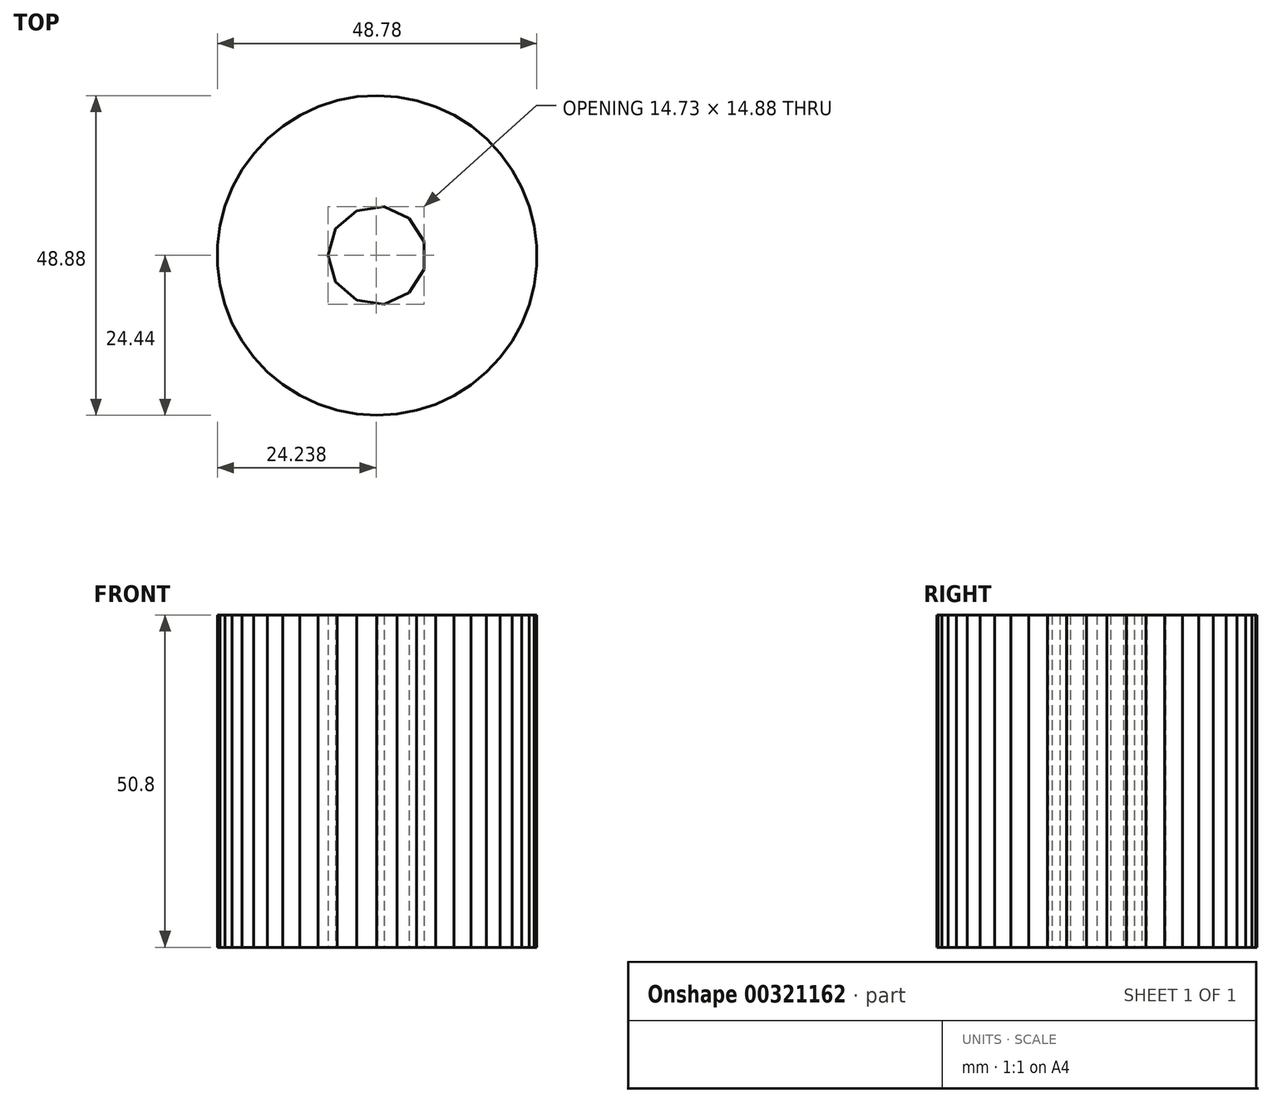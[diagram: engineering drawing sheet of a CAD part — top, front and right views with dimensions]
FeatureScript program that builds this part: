
annotation { "Feature Type Name" : "Feature", "Feature Type Description" : "" }
export const myFeature = defineFeature(function(context is Context, id is Id, definition is map)
    precondition{}
    {
        {
            var Q0;
            Q0=qCreatedBy(makeId("Top.planeOp"),FACE);
            var sketch = newSketch(context, id + "F0", { "sketchPlane" : qUnion([Q0])});
            skCircle(sketch, "E0.cCircle", {"center": v(0, 0) * mm, "radius": 24.4 * mm, "construction": true});
            skLineSegment(sketch, "E0.0", {"start": v(22.1, -10.44) * mm, "end": v(20.61, -13.13) * mm});
            skLineSegment(sketch, "E0.1", {"start": v(20.61, -13.13) * mm, "end": v(18.8, -15.61) * mm});
            skLineSegment(sketch, "E0.2", {"start": v(18.8, -15.61) * mm, "end": v(16.7, -17.84) * mm});
            skLineSegment(sketch, "E0.3", {"start": v(16.7, -17.84) * mm, "end": v(14.33, -19.8) * mm});
            skLineSegment(sketch, "E0.4", {"start": v(14.33, -19.8) * mm, "end": v(11.74, -21.44) * mm});
            skLineSegment(sketch, "E0.5", {"start": v(11.74, -21.44) * mm, "end": v(8.96, -22.74) * mm});
            skLineSegment(sketch, "E0.6", {"start": v(8.96, -22.74) * mm, "end": v(6.04, -23.68) * mm});
            skLineSegment(sketch, "E0.7", {"start": v(6.04, -23.68) * mm, "end": v(3.02, -24.25) * mm});
            skLineSegment(sketch, "E0.8", {"start": v(3.02, -24.25) * mm, "end": v(-0.04, -24.44) * mm});
            skLineSegment(sketch, "E0.9", {"start": v(-0.04, -24.44) * mm, "end": v(-3.1, -24.24) * mm});
            skLineSegment(sketch, "E0.10", {"start": v(-3.1, -24.24) * mm, "end": v(-6.12, -23.66) * mm});
            skLineSegment(sketch, "E0.11", {"start": v(-6.12, -23.66) * mm, "end": v(-9.04, -22.7) * mm});
            skLineSegment(sketch, "E0.12", {"start": v(-9.04, -22.7) * mm, "end": v(-11.8, -21.4) * mm});
            skLineSegment(sketch, "E0.13", {"start": v(-11.8, -21.4) * mm, "end": v(-14.4, -19.75) * mm});
            skLineSegment(sketch, "E0.14", {"start": v(-14.4, -19.75) * mm, "end": v(-16.76, -17.79) * mm});
            skLineSegment(sketch, "E0.15", {"start": v(-16.76, -17.79) * mm, "end": v(-18.86, -15.55) * mm});
            skLineSegment(sketch, "E0.16", {"start": v(-18.86, -15.55) * mm, "end": v(-20.66, -13.06) * mm});
            skLineSegment(sketch, "E0.17", {"start": v(-20.66, -13.06) * mm, "end": v(-22.13, -10.37) * mm});
            skLineSegment(sketch, "E0.18", {"start": v(-22.13, -10.37) * mm, "end": v(-23.26, -7.51) * mm});
            skLineSegment(sketch, "E0.19", {"start": v(-23.26, -7.51) * mm, "end": v(-24.01, -4.54) * mm});
            skLineSegment(sketch, "E0.20", {"start": v(-24.01, -4.54) * mm, "end": v(-24.4, -1.5) * mm});
            skLineSegment(sketch, "E0.21", {"start": v(-24.4, -1.5) * mm, "end": v(-24.39, 1.58) * mm});
            skLineSegment(sketch, "E0.22", {"start": v(-24.39, 1.58) * mm, "end": v(-24, 4.62) * mm});
            skLineSegment(sketch, "E0.23", {"start": v(-24, 4.62) * mm, "end": v(-23.23, 7.6) * mm});
            skLineSegment(sketch, "E0.24", {"start": v(-23.23, 7.6) * mm, "end": v(-22.1, 10.44) * mm});
            skLineSegment(sketch, "E0.25", {"start": v(-22.1, 10.44) * mm, "end": v(-20.61, 13.13) * mm});
            skLineSegment(sketch, "E0.26", {"start": v(-20.61, 13.13) * mm, "end": v(-18.8, 15.61) * mm});
            skLineSegment(sketch, "E0.27", {"start": v(-18.8, 15.61) * mm, "end": v(-16.7, 17.84) * mm});
            skLineSegment(sketch, "E0.28", {"start": v(-16.7, 17.84) * mm, "end": v(-14.33, 19.8) * mm});
            skLineSegment(sketch, "E0.29", {"start": v(-14.33, 19.8) * mm, "end": v(-11.74, 21.44) * mm});
            skLineSegment(sketch, "E0.30", {"start": v(-11.74, 21.44) * mm, "end": v(-8.96, 22.74) * mm});
            skLineSegment(sketch, "E0.31", {"start": v(-8.96, 22.74) * mm, "end": v(-6.04, 23.68) * mm});
            skLineSegment(sketch, "E0.32", {"start": v(-6.04, 23.68) * mm, "end": v(-3.02, 24.25) * mm});
            skLineSegment(sketch, "E0.33", {"start": v(-3.02, 24.25) * mm, "end": v(0.04, 24.44) * mm});
            skLineSegment(sketch, "E0.34", {"start": v(0.04, 24.44) * mm, "end": v(3.1, 24.24) * mm});
            skLineSegment(sketch, "E0.35", {"start": v(3.1, 24.24) * mm, "end": v(6.12, 23.66) * mm});
            skLineSegment(sketch, "E0.36", {"start": v(6.12, 23.66) * mm, "end": v(9.04, 22.7) * mm});
            skLineSegment(sketch, "E0.37", {"start": v(9.04, 22.7) * mm, "end": v(11.8, 21.4) * mm});
            skLineSegment(sketch, "E0.38", {"start": v(11.8, 21.4) * mm, "end": v(14.4, 19.75) * mm});
            skLineSegment(sketch, "E0.39", {"start": v(14.4, 19.75) * mm, "end": v(16.76, 17.79) * mm});
            skLineSegment(sketch, "E0.40", {"start": v(16.76, 17.79) * mm, "end": v(18.86, 15.55) * mm});
            skLineSegment(sketch, "E0.41", {"start": v(18.86, 15.55) * mm, "end": v(20.66, 13.06) * mm});
            skLineSegment(sketch, "E0.42", {"start": v(20.66, 13.06) * mm, "end": v(22.13, 10.37) * mm});
            skLineSegment(sketch, "E0.43", {"start": v(22.13, 10.37) * mm, "end": v(23.26, 7.51) * mm});
            skLineSegment(sketch, "E0.44", {"start": v(23.26, 7.51) * mm, "end": v(24.01, 4.54) * mm});
            skLineSegment(sketch, "E0.45", {"start": v(24.01, 4.54) * mm, "end": v(24.4, 1.5) * mm});
            skLineSegment(sketch, "E0.46", {"start": v(24.4, 1.5) * mm, "end": v(24.39, -1.58) * mm});
            skLineSegment(sketch, "E0.47", {"start": v(24.39, -1.58) * mm, "end": v(24, -4.62) * mm});
            skLineSegment(sketch, "E0.48", {"start": v(24, -4.62) * mm, "end": v(23.23, -7.6) * mm});
            skLineSegment(sketch, "E0.49", {"start": v(23.23, -7.6) * mm, "end": v(22.1, -10.44) * mm});
            skPoint(sketch, "E0.0.midPoint", {"position": v(21.35, -11.79) * mm});
            skCircle(sketch, "E1.cCircle", {"center": v(0, 0) * mm, "radius": 7.21 * mm, "construction": true});
            skLineSegment(sketch, "E1.0", {"start": v(7.21, 2.12) * mm, "end": v(7.21, -2.12) * mm});
            skLineSegment(sketch, "E1.1", {"start": v(7.21, -2.12) * mm, "end": v(4.92, -5.68) * mm});
            skLineSegment(sketch, "E1.2", {"start": v(4.92, -5.68) * mm, "end": v(1.07, -7.44) * mm});
            skLineSegment(sketch, "E1.3", {"start": v(1.07, -7.44) * mm, "end": v(-3.12, -6.84) * mm});
            skLineSegment(sketch, "E1.4", {"start": v(-3.12, -6.84) * mm, "end": v(-6.32, -4.06) * mm});
            skLineSegment(sketch, "E1.5", {"start": v(-6.32, -4.06) * mm, "end": v(-7.52, 0) * mm});
            skLineSegment(sketch, "E1.6", {"start": v(-7.52, 0) * mm, "end": v(-6.32, 4.06) * mm});
            skLineSegment(sketch, "E1.7", {"start": v(-6.32, 4.06) * mm, "end": v(-3.12, 6.84) * mm});
            skLineSegment(sketch, "E1.8", {"start": v(-3.12, 6.84) * mm, "end": v(1.07, 7.44) * mm});
            skLineSegment(sketch, "E1.9", {"start": v(1.07, 7.44) * mm, "end": v(4.92, 5.68) * mm});
            skLineSegment(sketch, "E1.10", {"start": v(4.92, 5.68) * mm, "end": v(7.21, 2.12) * mm});
            skPoint(sketch, "E1.0.midPoint", {"position": v(7.21, 0) * mm});
            skSolve(sketch);
        }
        {
            var Q0;
            Q0=makeQuery(id+"F0.imprint","IMPRINT",FACE,{"disambiguationData":[TD([[makeQuery(id+"F0.imprint","IMPRINT",EDGE,{"derivedFrom":sQuery(id+"F0.wireOp",EDGE,"E0.0")}),-1.0]])]});
            extrude(context, id + "F1", {"entities" : qUnion([Q0]), "depth" : 25.4 * mm});
        }
        {
            var Q0;
            Q0=makeQuery(id+"F1.opExtrude","CAP_FACE",FACE,{"disambiguationData":[OSD([sQuery(id+"F0.wireOp",EDGE,"E0.0"),sQuery(id+"F0.wireOp",EDGE,"E0.1"),sQuery(id+"F0.wireOp",EDGE,"E0.2"),sQuery(id+"F0.wireOp",EDGE,"E0.3"),sQuery(id+"F0.wireOp",EDGE,"E0.4"),sQuery(id+"F0.wireOp",EDGE,"E0.5"),sQuery(id+"F0.wireOp",EDGE,"E0.6"),sQuery(id+"F0.wireOp",EDGE,"E0.7"),sQuery(id+"F0.wireOp",EDGE,"E0.8"),sQuery(id+"F0.wireOp",EDGE,"E0.9"),sQuery(id+"F0.wireOp",EDGE,"E0.10"),sQuery(id+"F0.wireOp",EDGE,"E0.11"),sQuery(id+"F0.wireOp",EDGE,"E0.12"),sQuery(id+"F0.wireOp",EDGE,"E0.13"),sQuery(id+"F0.wireOp",EDGE,"E0.14"),sQuery(id+"F0.wireOp",EDGE,"E0.15"),sQuery(id+"F0.wireOp",EDGE,"E0.16"),sQuery(id+"F0.wireOp",EDGE,"E0.17"),sQuery(id+"F0.wireOp",EDGE,"E0.18"),sQuery(id+"F0.wireOp",EDGE,"E0.19"),sQuery(id+"F0.wireOp",EDGE,"E0.20"),sQuery(id+"F0.wireOp",EDGE,"E0.21"),sQuery(id+"F0.wireOp",EDGE,"E0.22"),sQuery(id+"F0.wireOp",EDGE,"E0.23"),sQuery(id+"F0.wireOp",EDGE,"E0.24"),sQuery(id+"F0.wireOp",EDGE,"E0.25"),sQuery(id+"F0.wireOp",EDGE,"E0.26"),sQuery(id+"F0.wireOp",EDGE,"E0.27"),sQuery(id+"F0.wireOp",EDGE,"E0.28"),sQuery(id+"F0.wireOp",EDGE,"E0.29"),sQuery(id+"F0.wireOp",EDGE,"E0.30"),sQuery(id+"F0.wireOp",EDGE,"E0.31"),sQuery(id+"F0.wireOp",EDGE,"E0.32"),sQuery(id+"F0.wireOp",EDGE,"E0.33"),sQuery(id+"F0.wireOp",EDGE,"E0.34"),sQuery(id+"F0.wireOp",EDGE,"E0.35"),sQuery(id+"F0.wireOp",EDGE,"E0.36"),sQuery(id+"F0.wireOp",EDGE,"E0.37"),sQuery(id+"F0.wireOp",EDGE,"E0.38"),sQuery(id+"F0.wireOp",EDGE,"E0.39"),sQuery(id+"F0.wireOp",EDGE,"E0.40"),sQuery(id+"F0.wireOp",EDGE,"E0.41"),sQuery(id+"F0.wireOp",EDGE,"E0.42"),sQuery(id+"F0.wireOp",EDGE,"E0.43"),sQuery(id+"F0.wireOp",EDGE,"E0.44"),sQuery(id+"F0.wireOp",EDGE,"E0.45"),sQuery(id+"F0.wireOp",EDGE,"E0.46"),sQuery(id+"F0.wireOp",EDGE,"E0.47"),sQuery(id+"F0.wireOp",EDGE,"E0.48"),sQuery(id+"F0.wireOp",EDGE,"E0.49"),sQuery(id+"F0.wireOp",EDGE,"E1.0"),sQuery(id+"F0.wireOp",EDGE,"E1.1"),sQuery(id+"F0.wireOp",EDGE,"E1.2"),sQuery(id+"F0.wireOp",EDGE,"E1.3"),sQuery(id+"F0.wireOp",EDGE,"E1.4"),sQuery(id+"F0.wireOp",EDGE,"E1.5"),sQuery(id+"F0.wireOp",EDGE,"E1.6"),sQuery(id+"F0.wireOp",EDGE,"E1.7"),sQuery(id+"F0.wireOp",EDGE,"E1.8"),sQuery(id+"F0.wireOp",EDGE,"E1.9"),sQuery(id+"F0.wireOp",EDGE,"E1.10")])],"isStart":false});
            extrude(context, id + "F2", {"entities" : qUnion([Q0]), "operationType" : NewBodyOperationType.ADD, "depth" : 25.4 * mm});
        }
    });
